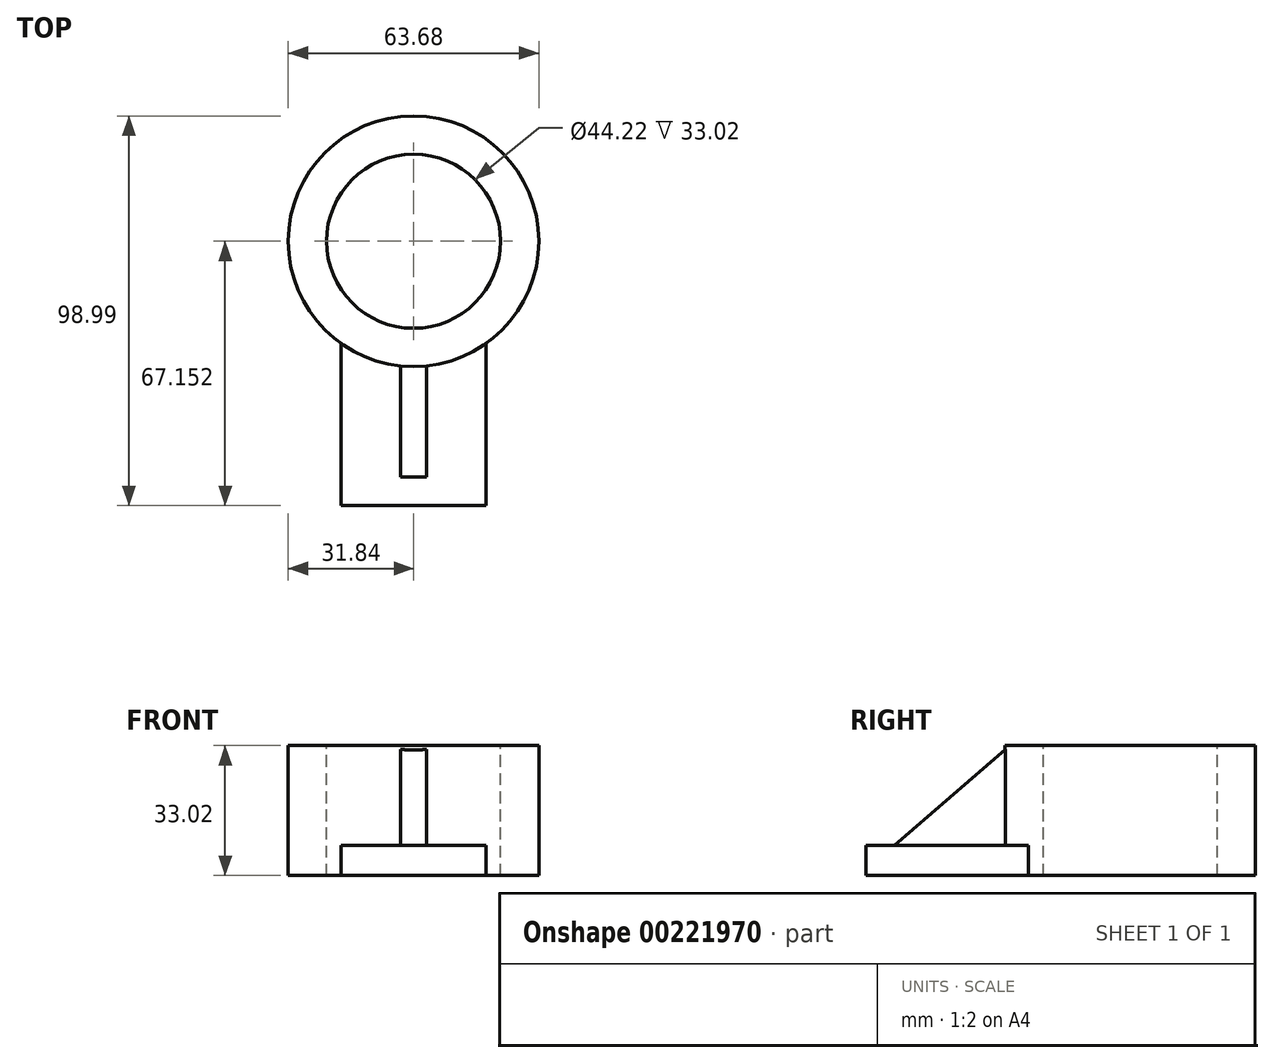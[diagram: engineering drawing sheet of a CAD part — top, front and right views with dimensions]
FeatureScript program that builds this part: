
annotation { "Feature Type Name" : "Feature", "Feature Type Description" : "" }
export const myFeature = defineFeature(function(context is Context, id is Id, definition is map)
    precondition{}
    {
        {
            var Q0;
            Q0=qCreatedBy(makeId("Top.planeOp"),FACE);
            var sketch = newSketch(context, id + "F0", { "sketchPlane" : qUnion([Q0])});
            skCircle(sketch, "E0", {"center": v(0, 31.6) * mm, "radius": 31.84 * mm});
            skCircle(sketch, "E1", {"center": v(0, 31.6) * mm, "radius": 22.11 * mm});
            skLineSegment(sketch, "E2", {"start": v(-18.47, 5.67) * mm, "end": v(-18.47, -35.55) * mm});
            skLineSegment(sketch, "E3", {"start": v(-18.47, -35.55) * mm, "end": v(0, -35.55) * mm});
            skLineSegment(sketch, "E4.MirrorCS", {"start": v(18.47, -35.55) * mm, "end": v(0, -35.55) * mm});
            skLineSegment(sketch, "E5.MirrorCS", {"start": v(18.47, 5.67) * mm, "end": v(18.47, -35.55) * mm});
            skSolve(sketch);
        }
        {
            var Q0;
            Q0 = qSketchRegion(id + "F0", true);
            extrude(context, id + "F1", {"entities" : qUnion([Q0]), "oppositeDirection" : true, "depth" : 7.62 * mm});
        }
        {
            var Q0;
            Q0=makeQuery(id+"F0.imprint","IMPRINT",FACE,{"disambiguationData":[TD([[makeQuery(id+"F0.imprint","IMPRINT",EDGE,{"derivedFrom":sQuery(id+"F0.wireOp",EDGE,"E1")}),-1.0]])]});
            extrude(context, id + "F2", {"entities" : qUnion([Q0]), "operationType" : NewBodyOperationType.ADD, "depth" : 25.4 * mm});
        }
        {
            var Q0;
            Q0=qCreatedBy(makeId("Right.planeOp"),FACE);
            var sketch = newSketch(context, id + "F3", { "sketchPlane" : qUnion([Q0])});
            skLineSegment(sketch, "E6", {"start": v(-28.3, 0) * mm, "end": v(3.35, 0) * mm});
            skLineSegment(sketch, "E7", {"start": v(-28.3, 0) * mm, "end": v(0, 24.5) * mm});
            skLineSegment(sketch, "E8", {"start": v(3.35, 0) * mm, "end": v(3.35, 24.5) * mm});
            skLineSegment(sketch, "E9", {"start": v(3.35, 24.5) * mm, "end": v(0, 24.5) * mm});
            skSolve(sketch);
        }
        {
            var Q0;
            Q0 = qSketchRegion(id + "F3", true);
            extrude(context, id + "F4", {"entities" : qUnion([Q0]), "operationType" : NewBodyOperationType.ADD, "endBound" : BoundingType.SYMMETRIC, "depth" : 6.6 * mm});
        }
    });
